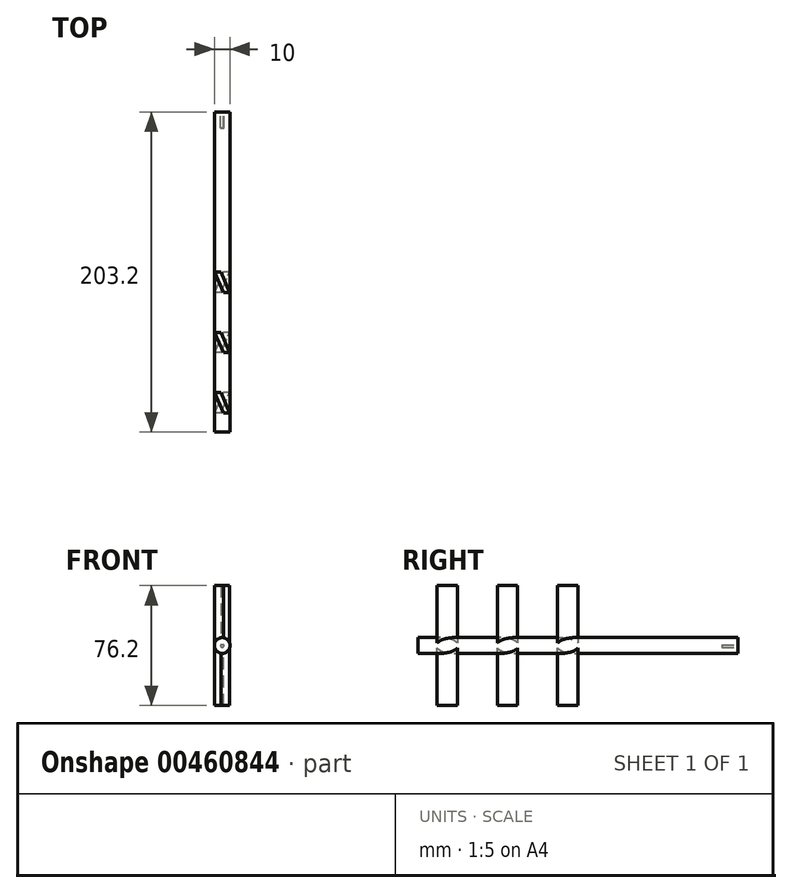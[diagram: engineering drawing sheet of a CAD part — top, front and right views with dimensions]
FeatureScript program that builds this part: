
annotation { "Feature Type Name" : "Feature", "Feature Type Description" : "" }
export const myFeature = defineFeature(function(context is Context, id is Id, definition is map)
    precondition{}
    {
        {
            var Q0;
            Q0=qCreatedBy(makeId("Front.planeOp"),FACE);
            var sketch = newSketch(context, id + "F0", { "sketchPlane" : qUnion([Q0])});
            skCircle(sketch, "E0", {"center": v(0, 0) * mm, "radius": 5 * mm});
            skSolve(sketch);
        }
        {
            var Q0;
            Q0=qSketchRegion(id+"F0",true);
            extrude(context, id + "F1", {"entities" : qUnion([Q0]), "depth" : 203.2 * mm});
        }
        {
            var Q0;
            Q0=qCreatedBy(makeId("Top.planeOp"),FACE);
            var sketch = newSketch(context, id + "F2", { "sketchPlane" : qUnion([Q0])});
            skPoint(sketch, "E1", {"position": v(0, 0) * mm});
            skLineSegment(sketch, "E2.bottom", {"start": v(4.74, -114.49) * mm, "end": v(0.74, -114.49) * mm});
            skLineSegment(sketch, "E2.top", {"start": v(-0.74, -101.6) * mm, "end": v(-4.74, -101.6) * mm});
            skLineSegment(sketch, "E2.left", {"start": v(4.74, -114.49) * mm, "end": v(-0.74, -101.6) * mm});
            skLineSegment(sketch, "E2.right", {"start": v(0.74, -114.49) * mm, "end": v(-4.74, -101.6) * mm});
            skPoint(sketch, "E2.middle", {"position": v(0, -108.04) * mm});
            skLineSegment(sketch, "E3.bottom", {"start": v(-0.74, -139.89) * mm, "end": v(-4.74, -139.89) * mm});
            skLineSegment(sketch, "E3.top", {"start": v(4.74, -152.77) * mm, "end": v(0.74, -152.77) * mm});
            skLineSegment(sketch, "E3.left", {"start": v(-0.74, -139.89) * mm, "end": v(4.74, -152.77) * mm});
            skLineSegment(sketch, "E3.right", {"start": v(-4.74, -139.89) * mm, "end": v(0.74, -152.77) * mm});
            skPoint(sketch, "E3.middle", {"position": v(0, -146.33) * mm});
            skLineSegment(sketch, "E4.bottom", {"start": v(-0.74, -178.17) * mm, "end": v(-4.74, -178.17) * mm});
            skLineSegment(sketch, "E4.top", {"start": v(4.74, -191.06) * mm, "end": v(0.74, -191.06) * mm});
            skLineSegment(sketch, "E4.left", {"start": v(-0.74, -178.17) * mm, "end": v(4.74, -191.06) * mm});
            skLineSegment(sketch, "E4.right", {"start": v(-4.74, -178.17) * mm, "end": v(0.74, -191.06) * mm});
            skPoint(sketch, "E4.middle", {"position": v(0, -184.62) * mm});
            skLineSegment(sketch, "E5", {"start": v(0, -114.49) * mm, "end": v(0, -139.89) * mm, "construction": true});
            skLineSegment(sketch, "E6", {"start": v(0, -152.77) * mm, "end": v(0, -178.17) * mm, "construction": true});
            skSolve(sketch);
        }
        {
            var Q0;
            Q0=qSketchRegion(id+"F2",true);
            extrude(context, id + "F3", {"entities" : qUnion([Q0]), "operationType" : NewBodyOperationType.ADD, "depth" : 38.1 * mm});
        }
        {
            var Q0;
            Q0=qCreatedBy(makeId("Top.planeOp"),FACE);
            var sketch = newSketch(context, id + "F4", { "sketchPlane" : qUnion([Q0])});
            skLineSegment(sketch, "E7.bottom", {"start": v(-0.74, -114.49) * mm, "end": v(-4.74, -114.49) * mm});
            skLineSegment(sketch, "E7.top", {"start": v(4.74, -101.6) * mm, "end": v(0.74, -101.6) * mm});
            skLineSegment(sketch, "E7.left", {"start": v(-0.74, -114.49) * mm, "end": v(4.74, -101.6) * mm});
            skLineSegment(sketch, "E7.right", {"start": v(-4.74, -114.49) * mm, "end": v(0.74, -101.6) * mm});
            skPoint(sketch, "E7.middle", {"position": v(0, -108.04) * mm});
            skLineSegment(sketch, "E8.bottom", {"start": v(-0.74, -152.77) * mm, "end": v(-4.74, -152.77) * mm});
            skLineSegment(sketch, "E8.top", {"start": v(4.74, -139.89) * mm, "end": v(0.74, -139.89) * mm});
            skLineSegment(sketch, "E8.left", {"start": v(-0.74, -152.77) * mm, "end": v(4.74, -139.89) * mm});
            skLineSegment(sketch, "E8.right", {"start": v(-4.74, -152.77) * mm, "end": v(0.74, -139.89) * mm});
            skPoint(sketch, "E8.middle", {"position": v(0, -146.33) * mm});
            skLineSegment(sketch, "E9.bottom", {"start": v(-0.74, -191.06) * mm, "end": v(-4.74, -191.06) * mm});
            skLineSegment(sketch, "E9.top", {"start": v(4.74, -178.17) * mm, "end": v(0.74, -178.17) * mm});
            skLineSegment(sketch, "E9.left", {"start": v(-0.74, -191.06) * mm, "end": v(4.74, -178.17) * mm});
            skLineSegment(sketch, "E9.right", {"start": v(-4.74, -191.06) * mm, "end": v(0.74, -178.17) * mm});
            skPoint(sketch, "E9.middle", {"position": v(0, -184.62) * mm});
            skLineSegment(sketch, "E10", {"start": v(0, -178.17) * mm, "end": v(0, -152.77) * mm, "construction": true});
            skLineSegment(sketch, "E11", {"start": v(0, -139.89) * mm, "end": v(0, -114.49) * mm, "construction": true});
            skSolve(sketch);
        }
        {
            var Q0;
            Q0 = qSketchRegion(id + "F4", true);
            extrude(context, id + "F5", {"entities" : qUnion([Q0]), "operationType" : NewBodyOperationType.ADD, "oppositeDirection" : true, "depth" : 38.1 * mm});
        }
        {
            var Q0;
            Q0=qCreatedBy(makeId("Front.planeOp"),FACE);
            var sketch = newSketch(context, id + "F6", { "sketchPlane" : qUnion([Q0])});
            skArc(sketch, "E12", {"start": v(-1, 0.42) * mm, "mid": v(0, -1.08) * mm, "end": v(1, 0.42) * mm});
            skLineSegment(sketch, "E13", {"start": v(1, 0.42) * mm, "end": v(-1, 0.42) * mm});
            skPoint(sketch, "E14", {"position": v(0, 0.42) * mm});
            skPoint(sketch, "E15", {"position": v(0, -1.08) * mm});
            skSolve(sketch);
        }
        {
            var Q0;
            Q0 = qSketchRegion(id + "F6", true);
            extrude(context, id + "F7", {"entities" : qUnion([Q0]), "operationType" : NewBodyOperationType.REMOVE, "depth" : 10 * mm});
        }
    });
